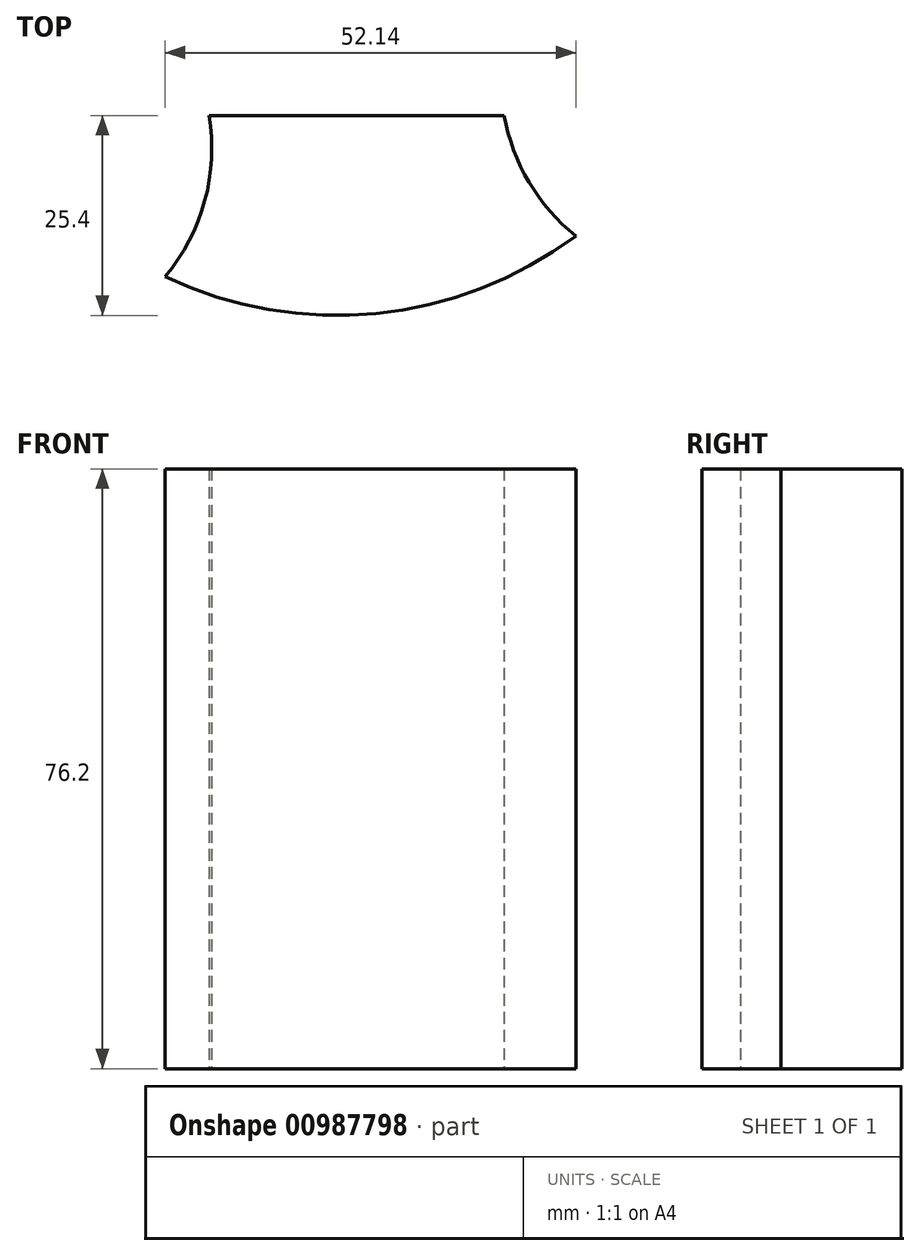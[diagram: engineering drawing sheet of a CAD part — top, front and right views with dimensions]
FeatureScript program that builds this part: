
annotation { "Feature Type Name" : "Feature", "Feature Type Description" : "" }
export const myFeature = defineFeature(function(context is Context, id is Id, definition is map)
    precondition{}
    {
        {
            var Q0;
            Q0=qCreatedBy(makeId("Top.planeOp"),FACE);
            var sketch = newSketch(context, id + "F0", { "sketchPlane" : qUnion([Q0])});
            skCircle(sketch, "E0", {"center": v(0, 0) * mm, "radius": 50.8 * mm});
            skLineSegment(sketch, "E1.bottom", {"start": v(25.4, -25.4) * mm, "end": v(-25.4, -25.4) * mm});
            skLineSegment(sketch, "E1.top", {"start": v(25.4, 25.4) * mm, "end": v(-25.4, 25.4) * mm});
            skLineSegment(sketch, "E1.left", {"start": v(25.4, -25.4) * mm, "end": v(25.4, 25.4) * mm});
            skLineSegment(sketch, "E1.right", {"start": v(-25.4, -25.4) * mm, "end": v(-25.4, 25.4) * mm});
            skCircle(sketch, "E2", {"center": v(46.29, -20.93) * mm, "radius": 25.4 * mm});
            skLineSegment(sketch, "E3", {"start": v(66.92, -6.12) * mm, "end": v(41.27, 29.62) * mm});
            skLineSegment(sketch, "E4", {"start": v(48.8, -46.2) * mm, "end": v(5.02, -50.55) * mm});
            skLineSegment(sketch, "E5.1.0", {"start": v(-28.16, 61.02) * mm, "end": v(-46.29, 20.93) * mm});
            skLineSegment(sketch, "E5.1.1", {"start": v(15.62, 65.36) * mm, "end": v(41.27, 29.62) * mm});
            skCircle(sketch, "E5.1.2", {"center": v(-5.02, 50.55) * mm, "radius": 25.4 * mm});
            skLineSegment(sketch, "E5.2.0", {"start": v(-38.76, -54.9) * mm, "end": v(5.02, -50.55) * mm});
            skLineSegment(sketch, "E5.2.1", {"start": v(-64.41, -19.15) * mm, "end": v(-46.29, 20.93) * mm});
            skCircle(sketch, "E5.2.2", {"center": v(-41.27, -29.62) * mm, "radius": 25.4 * mm});
            skSolve(sketch);
        }
        {
            var Q0;
            Q0=makeQuery(id+"F0.imprint","IMPRINT",FACE,{"disambiguationData":[TD([[makeQuery(id+"F0.imprint","IMPRINT",EDGE,{"derivedFrom":sQuery(id+"F0.wireOp",EDGE,"E0")}),1.0]])]});
            extrude(context, id + "F1", {"entities" : qUnion([Q0]), "depth" : 76.2 * mm, "offsetDistance" : 25.4 * mm});
        }
    });
